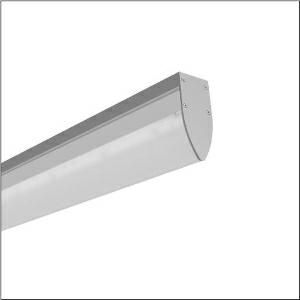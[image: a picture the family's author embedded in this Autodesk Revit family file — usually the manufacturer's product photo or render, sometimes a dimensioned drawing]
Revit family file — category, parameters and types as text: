
# Revit family: mira_r__21_td_51fr527p494a_f38a
name_source: partatom
category: Lighting Fixtures
units: mm (PartAtom-declared; Revit-internal decimal feet)

## family parameters
Cut with Voids When Loaded = No
Host = Face
Light Source = No
Part Type = Normal
Room Calculation Point = No
Round Connector Dimension = Use Diameter
Shared = No

## types (1)
- Mira® 21 TD (1 x LED, 9160 lm, 65 W, 4000K)
    Apparent Load = 65 VA
    CIE Flux Codes = 40 68 87 81 100
    Color Rendering = 80
    Color Temperature = 4000K
    Default Elevation = 1800 mm
    Description = Mira® 21 TD, clean room luminaire, primary light control with reflector, primary optical cover: cover, of PMMA, frosted, light emission: direct distribution, primary light characteristic: symmetric, installation type: surface-mounted, LED, rated luminous flux: 9.160lm, luminous efficacy: 141lm/W, light colour: 840, colour temperature: 4000K, control gear: ECG, with terminal, 3-pole, max. 2.5mm², mains connection: 230V, AC, 50/60Hz, rated input power: 65W, luminaire housing, of sheet steel, coated, pure white, length: 1.500mm, width: 55mm, height: 120mm, protection rating (complete): IP43, insulation class (complete): insulation class I (protective earthing), certification: CE, UKCA, permissible operating ambient temperature: -5..+40°C, standard: EN 50419, packaging unit: 1 piece
    Height = 0 mm  [stored 0 ft]
    Lamp = 1 x LED
    Lamp Light Flux = 9160 lm
    Lamp Power = 65 W
    Lamp count = 1
    Length = 1500 mm
    Luminous efficacy = 141 lm/W
    Manufacturer = Siteco
    ModVariant = No
    Model = 51FR527P494A
    Mounting Place = Ceiling
    Mounting Type = Recessed
    Number of Poles = 1
    OnlyDefault = Yes
    Power Factor = 1
    Product Name = Mira® 21 TD
    Product group = clean room luminaire
    ProductGroupID = 401
    Protection Class = Protection class I
    Protection Degree = IP 43
    RLX_Detail_Level = 1
    RlxData = <blob elided: 25169 chars, md5=55b4bc7e>
    Socket = socket
    Standby Power = 0 W
    System Light Flux = 9160 lm
    System Power = 65 W
    Type Comments = Product without accessories
    Type Image = l_1007115.jpg
    URL = http://relux.com
    VarID = ---
    Voltage = 0 V
    Weight = 0.00 kg
    Width = 55 mm

note: [stored X ft] marks values corroborated as IEEE doubles in the binary element streams (Revit-internal decimal feet)

## geometry (parser evidence)
native form markers: Blend x4, Sweep x13
no freeform markers — native parametric forms only
